# Revit family: Haworth_Janus_Accessories_Pillows_Square
name_source: partatom
category: Furniture
revit_build: Autodesk Revit 2018 (Build: 20170223_1515(x64)
units: mm (PartAtom-declared; Revit-internal decimal feet)

## family parameters
Always vertical = Yes
Cut with Voids When Loaded = No
OmniClass Number = 23.40.20.00
OmniClass Title = General Furniture and Specialties
Room Calculation Point = No
Shared = No
Work Plane-Based = No

## types (9) — shared parameters
Actual Depth = 5"
Assembly Code = E2020200
Manufacturer = Haworth
Size = Verify Final Dim. w/ Haworth
Sustainability Info = https://www.haworth.com
URL = http://www.haworth.com
URL - Product = https://www.haworth.com
Version = 1
Warranty = http://www.haworth.com

## per-type parameters (varying)
| type | Actual Height | Actual Width | Description | HeightCore | Pillow Offset | WidthCore |
| HCJC-JP-P1212 | 12" | 12" | Haworth - Janus - Pillows - 12 x 12 | 15/16" | 21 229/256" | 15/16" |
| HCJC-JP-P1414 | 14" | 14" | Haworth - Janus - Pillows - 14 x 14 | 2 15/16" | 21 229/256" | 2 15/16" |
| HCJC-JP-P1616 | 16" | 16" | Haworth - Janus - Pillows - 16 x 16 | 4 15/16" | 21 229/256" | 4 15/16" |
| HCJC-JP-P1818 | 18" | 18" | Haworth - Janus - Pillows - 18 x 18 | 6 15/16" | 21 229/256" | 6 15/16" |
| HCJC-JP-P1717 | 17" | 17" | Haworth - Janus - Pillows - 17 x 17 | 5 15/16" | 21 229/256" | 5 15/16" |
| HCJC-JP-P2020 | 20" | 20" | Haworth - Janus - Pillows - 20 x 20 | 8 15/16" | 21 229/256" | 8 15/16" |
| HCJC-JP-P2222 | 22" | 22" | Haworth - Janus - Pillows - 22 x 22 | 10 15/16" | 21 229/256" | 10 15/16" |
| HCJC-JP-P2424 | 24" | 24" | Haworth - Janus - Pillows - 24 x 24 | 12 15/16" | 21 229/256" | 12 15/16" |
| HCJC-JP-P3030 | 30" | 30" | Haworth - Janus - Pillows - 30 x 30 | 18 15/16" | 17" | 18 15/16" |

note: column(s) folded — value = type name in every type: Model

## geometry (parser evidence)
native form markers: Sweep x2
no freeform markers — native parametric forms only
